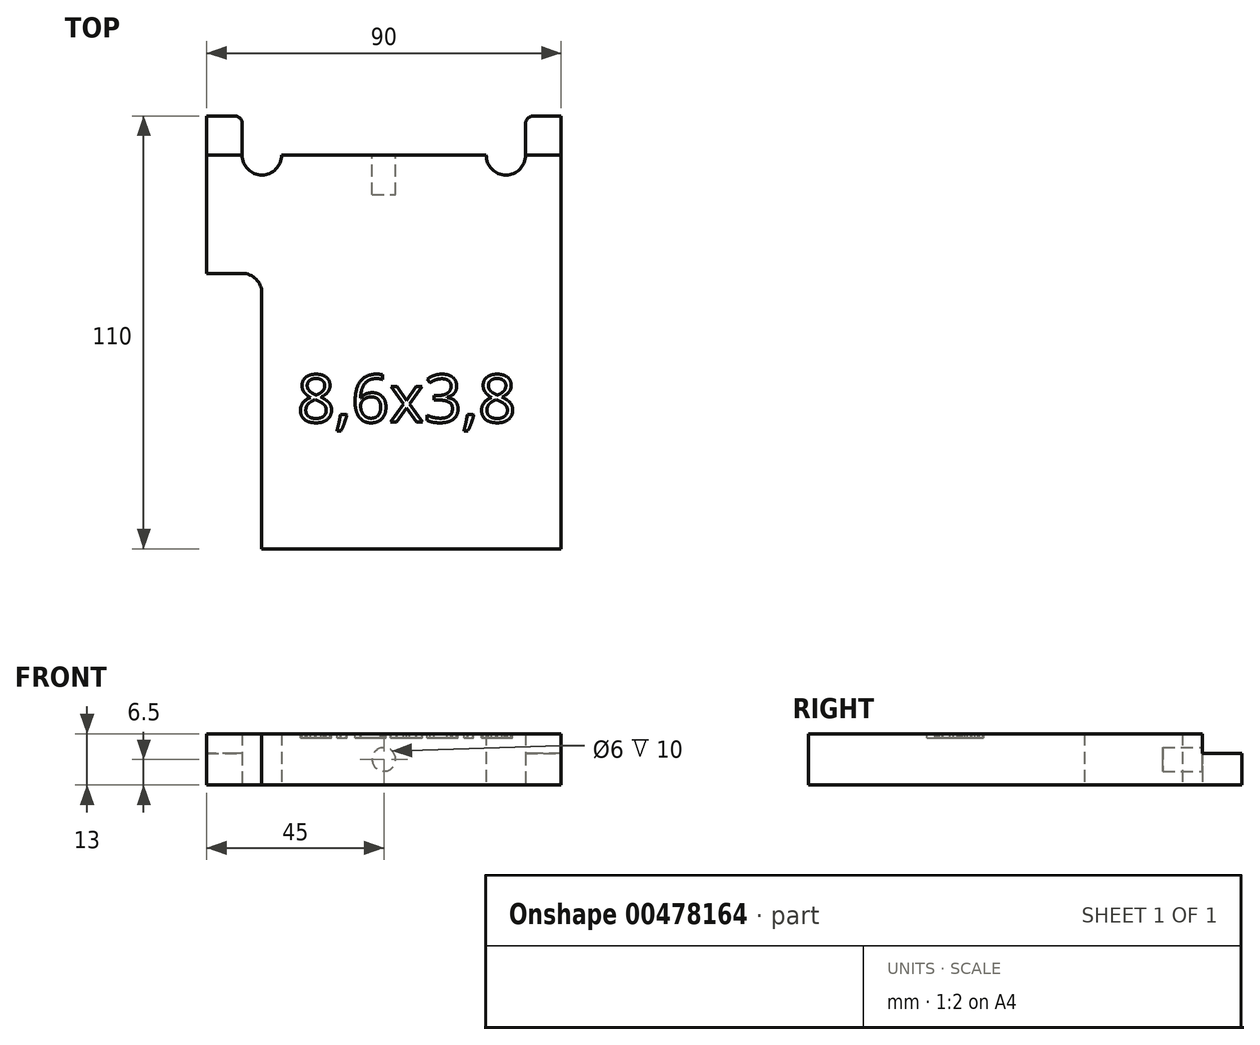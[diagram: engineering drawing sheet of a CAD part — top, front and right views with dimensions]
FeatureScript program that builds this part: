
annotation { "Feature Type Name" : "Feature", "Feature Type Description" : "" }
export const myFeature = defineFeature(function(context is Context, id is Id, definition is map)
    precondition{}
    {
        {
            var Q0;
            Q0=qCreatedBy(makeId("Top.planeOp"),FACE);
            var sketch = newSketch(context, id + "F0", { "sketchPlane" : qUnion([Q0])});
            skLineSegment(sketch, "E0", {"start": v(-41.48, -10.08) * mm, "end": v(-32.51, -10.08) * mm});
            skLineSegment(sketch, "E1", {"start": v(-27.51, -15.08) * mm, "end": v(-27.51, -80.08) * mm});
            skLineSegment(sketch, "E2", {"start": v(-27.51, -80.08) * mm, "end": v(48.52, -80.08) * mm});
            skLineSegment(sketch, "E3", {"start": v(48.52, -80.08) * mm, "end": v(48.52, 29.92) * mm});
            skLineSegment(sketch, "E4", {"start": v(48.52, 29.92) * mm, "end": v(41.52, 29.92) * mm});
            skLineSegment(sketch, "E5", {"start": v(39.52, 27.92) * mm, "end": v(39.52, 19.92) * mm});
            skLineSegment(sketch, "E6", {"start": v(-32.48, 19.92) * mm, "end": v(-32.48, 27.92) * mm});
            skLineSegment(sketch, "E7", {"start": v(-34.48, 29.92) * mm, "end": v(-41.48, 29.92) * mm});
            skLineSegment(sketch, "E8", {"start": v(-41.48, 29.92) * mm, "end": v(-41.48, -10.08) * mm});
            skPoint(sketch, "E9.visualSharp", {"position": v(-27.51, -10.08) * mm});
            skArc(sketch, "E9.filletArc", {"start": v(-27.51, -15.08) * mm, "mid": v(-28.97, -11.54) * mm, "end": v(-32.51, -10.08) * mm});
            skPoint(sketch, "E10.visualSharp", {"position": v(-32.48, 29.92) * mm});
            skArc(sketch, "E10.filletArc", {"start": v(-32.48, 27.92) * mm, "mid": v(-33.07, 29.33) * mm, "end": v(-34.48, 29.92) * mm});
            skPoint(sketch, "E11.visualSharp", {"position": v(39.52, 29.92) * mm});
            skArc(sketch, "E11.filletArc", {"start": v(41.52, 29.92) * mm, "mid": v(40.1, 29.33) * mm, "end": v(39.52, 27.92) * mm});
            skArc(sketch, "E12", {"start": v(-32.48, 19.92) * mm, "mid": v(-27.48, 14.92) * mm, "end": v(-22.48, 19.92) * mm});
            skArc(sketch, "E13", {"start": v(29.52, 19.92) * mm, "mid": v(34.52, 14.92) * mm, "end": v(39.52, 19.92) * mm});
            skLineSegment(sketch, "E14", {"start": v(-22.48, 19.92) * mm, "end": v(29.52, 19.92) * mm});
            skSolve(sketch);
        }
        {
            var Q0;
            Q0=makeQuery(id+"F0.imprint","IMPRINT",FACE,{"disambiguationData":[TD([[makeQuery(id+"F0.imprint","IMPRINT",EDGE,{"derivedFrom":sQuery(id+"F0.wireOp",EDGE,"E0")}),1.0]])]});
            extrude(context, id + "F1", {"entities" : qUnion([Q0]), "depth" : 13 * mm});
        }
        {
            var Q0;
            Q0=makeQuery(id+"F1.opExtrude","CAP_FACE",FACE,{"disambiguationData":[OSD([sQuery(id+"F0.wireOp",EDGE,"E0"),sQuery(id+"F0.wireOp",EDGE,"E1"),sQuery(id+"F0.wireOp",EDGE,"E2"),sQuery(id+"F0.wireOp",EDGE,"E3"),sQuery(id+"F0.wireOp",EDGE,"E4"),sQuery(id+"F0.wireOp",EDGE,"E5"),sQuery(id+"F0.wireOp",EDGE,"mmM2Y2U2-RtFC-ikFc-wxJO-fWfLtijxp1iX"),sQuery(id+"F0.wireOp",EDGE,"E6"),sQuery(id+"F0.wireOp",EDGE,"E7"),sQuery(id+"F0.wireOp",EDGE,"E8"),sQuery(id+"F0.wireOp",EDGE,"E9.filletArc"),sQuery(id+"F0.wireOp",EDGE,"E10.filletArc"),sQuery(id+"F0.wireOp",EDGE,"E11.filletArc")])],"isStart":false});
            var sketch = newSketch(context, id + "F2", { "sketchPlane" : qUnion([Q0])});
            skLineSegment(sketch, "E15.bottom", {"start": v(-43.08, 34.42) * mm, "end": v(64.23, 34.42) * mm});
            skLineSegment(sketch, "E15.top", {"start": v(-43.08, 19.92) * mm, "end": v(64.23, 19.92) * mm});
            skLineSegment(sketch, "E15.left", {"start": v(-43.08, 34.42) * mm, "end": v(-43.08, 19.92) * mm});
            skLineSegment(sketch, "E15.right", {"start": v(64.23, 34.42) * mm, "end": v(64.23, 19.92) * mm});
            skSolve(sketch);
        }
        {
            var Q0;
            Q0=qSketchRegion(id+"F2",true);
            extrude(context, id + "F3", {"entities" : qUnion([Q0]), "operationType" : NewBodyOperationType.REMOVE, "oppositeDirection" : true, "depth" : 5 * mm});
        }
        {
            var Q0;
            Q0=makeQuery(id+"F1.opExtrude","SWEPT_FACE",FACE,{"disambiguationData":[OSD([sQuery(id+"F0.wireOp",EDGE,"E14")])]});
            var sketch = newSketch(context, id + "F4", { "sketchPlane" : qUnion([Q0])});
            skCircle(sketch, "E16", {"center": v(-3.52, 6.5) * mm, "radius": 3 * mm});
            skSolve(sketch);
        }
        {
            var Q0;
            Q0=qSketchRegion(id+"F4",true);
            extrude(context, id + "F5", {"entities" : qUnion([Q0]), "operationType" : NewBodyOperationType.REMOVE, "oppositeDirection" : true, "depth" : 10 * mm});
        }
        {
            var Q0;
            Q0=makeQuery(id+"F1.opExtrude","CAP_FACE",FACE,{"disambiguationData":[OSD([sQuery(id+"F0.wireOp",EDGE,"E0"),sQuery(id+"F0.wireOp",EDGE,"E1"),sQuery(id+"F0.wireOp",EDGE,"E2"),sQuery(id+"F0.wireOp",EDGE,"E3"),sQuery(id+"F0.wireOp",EDGE,"E4"),sQuery(id+"F0.wireOp",EDGE,"E5"),sQuery(id+"F0.wireOp",EDGE,"E6"),sQuery(id+"F0.wireOp",EDGE,"E7"),sQuery(id+"F0.wireOp",EDGE,"E8"),sQuery(id+"F0.wireOp",EDGE,"E9.filletArc"),sQuery(id+"F0.wireOp",EDGE,"E10.filletArc"),sQuery(id+"F0.wireOp",EDGE,"E11.filletArc"),sQuery(id+"F0.wireOp",EDGE,"E12"),sQuery(id+"F0.wireOp",EDGE,"E13"),sQuery(id+"F0.wireOp",EDGE,"E14")])],"isStart":false});
            var sketch = newSketch(context, id + "F6", { "sketchPlane" : qUnion([Q0])});
            skText(sketch, "E17", { "text": "8,6x3,8", "fontName": "OpenSans-Regular.ttf"});
            const initialGuessF6  = {"E17": [-0.01854, -0.0479, 1, 0, 0.01214]};
            skSetInitialGuess(sketch, initialGuessF6);
            skSolve(sketch);
        }
        {
            var Q0;
            Q0=qSketchRegion(id+"F6",true);
            extrude(context, id + "F7", {"entities" : qUnion([Q0]), "operationType" : NewBodyOperationType.REMOVE, "oppositeDirection" : true, "depth" : 1 * mm});
        }
    });
